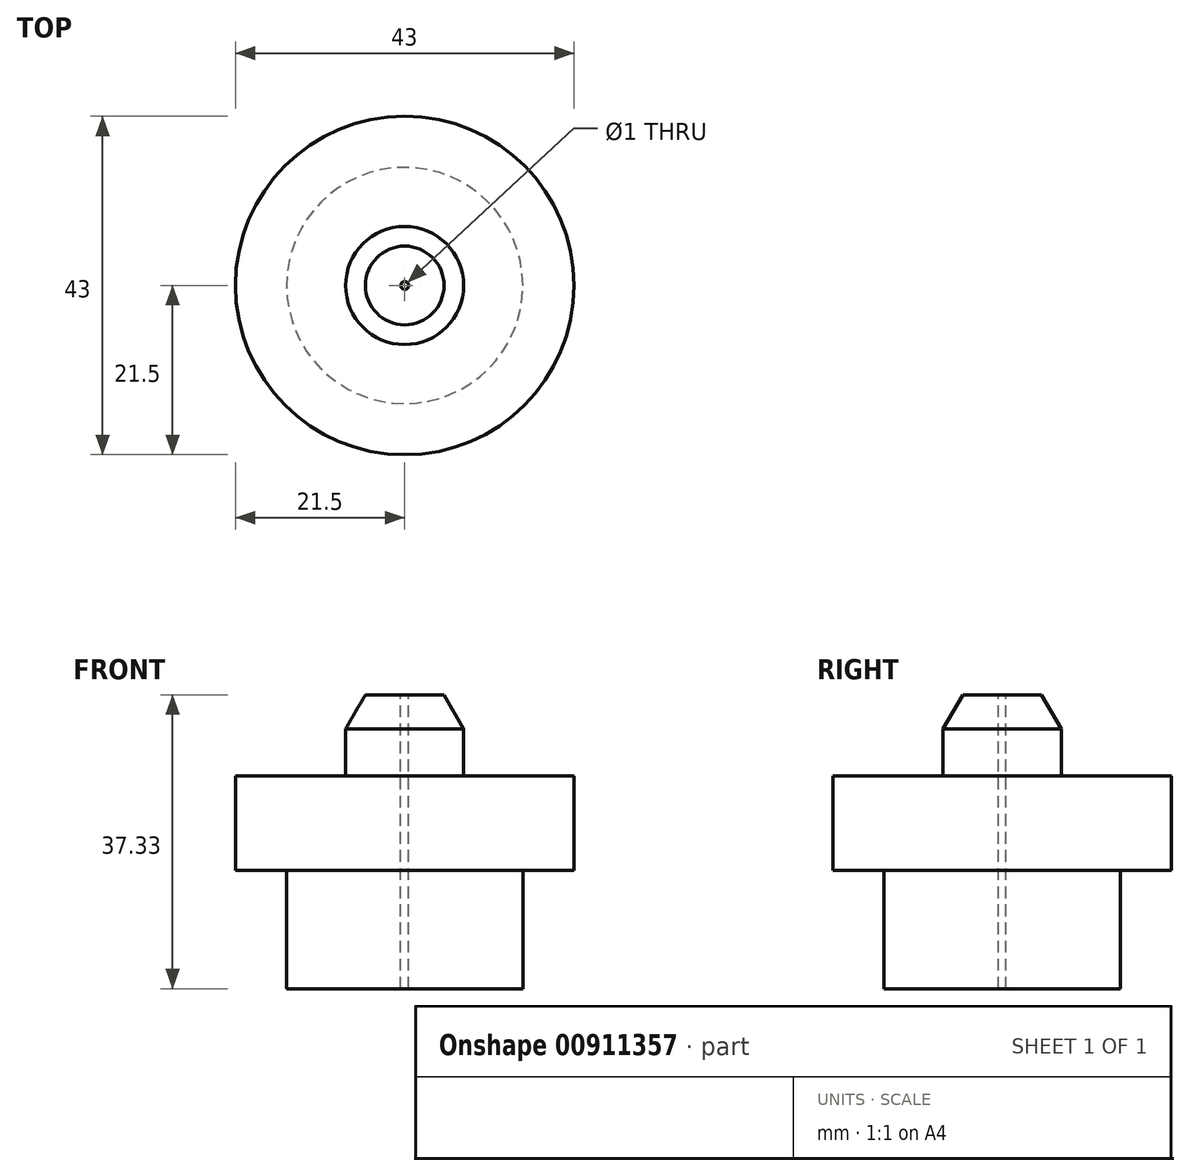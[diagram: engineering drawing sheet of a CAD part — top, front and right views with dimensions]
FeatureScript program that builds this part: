
annotation { "Feature Type Name" : "Feature", "Feature Type Description" : "" }
export const myFeature = defineFeature(function(context is Context, id is Id, definition is map)
    precondition{}
    {
        {
            var Q0;
            Q0=qCreatedBy(makeId("Front.planeOp"),FACE);
            var sketch = newSketch(context, id + "F0", { "sketchPlane" : qUnion([Q0])});
            skLineSegment(sketch, "E0", {"start": v(0, 0) * mm, "end": v(0, 94.63) * mm, "construction": true});
            skLineSegment(sketch, "E1", {"start": v(0, 37.33) * mm, "end": v(-5, 37.33) * mm});
            skLineSegment(sketch, "E2", {"start": v(-5, 37.33) * mm, "end": v(-7.5, 33) * mm});
            skLineSegment(sketch, "E3", {"start": v(-7.5, 33) * mm, "end": v(-7.5, 27) * mm});
            skLineSegment(sketch, "E4", {"start": v(-7.5, 27) * mm, "end": v(-21.5, 27) * mm});
            skLineSegment(sketch, "E5", {"start": v(-21.5, 27) * mm, "end": v(-21.5, 15) * mm});
            skLineSegment(sketch, "E6", {"start": v(-21.5, 15) * mm, "end": v(-15, 15) * mm});
            skLineSegment(sketch, "E7", {"start": v(-15, 15) * mm, "end": v(-15, 0) * mm});
            skLineSegment(sketch, "E8", {"start": v(-15, 0) * mm, "end": v(0, 0) * mm});
            skLineSegment(sketch, "E9", {"start": v(0, 37.33) * mm, "end": v(0, 0) * mm});
            skSolve(sketch);
        }
        {
            var Q0;
            Q0=makeQuery(id+"F0.imprint","IMPRINT",FACE,{"disambiguationData":[TD([[makeQuery(id+"F0.imprint","IMPRINT",EDGE,{"derivedFrom":sQuery(id+"F0.wireOp",EDGE,"E1")}),1.0]])]});
            var Q1;
            Q1=sQuery(id+"F0.wireOp",EDGE,"E0");
            revolve(context, id + "F1", {"surfaceOperationType" : NewSurfaceOperationType.NEW, "entities" : qUnion([Q0]), "axis" : qUnion([Q1]), "revolveType" : RevolveType.FULL});
        }
        {
            var Q0;
            Q0=makeQuery(id+"F1.opRevolve","SWEPT_FACE",FACE,{"disambiguationData":[OSD([sQuery(id+"F0.wireOp",EDGE,"E1")])]});
            var sketch = newSketch(context, id + "F2", { "sketchPlane" : qUnion([Q0])});
            skCircle(sketch, "E10", {"center": v(0, 0) * mm, "radius": 0.5 * mm});
            skSolve(sketch);
        }
        {
            var Q0;
            Q0=makeQuery(id+"F2.imprint","IMPRINT",FACE,{"disambiguationData":[TD([[makeQuery(id+"F2.imprint","IMPRINT",EDGE,{"derivedFrom":sQuery(id+"F2.wireOp",EDGE,"E10")}),1.0]])]});
            extrude(context, id + "F3", {"entities" : qUnion([Q0]), "operationType" : NewBodyOperationType.REMOVE, "endBound" : BoundingType.THROUGH_ALL, "oppositeDirection" : true, "depth" : 25 * mm, "offsetDistance" : 25 * mm});
        }
    });
